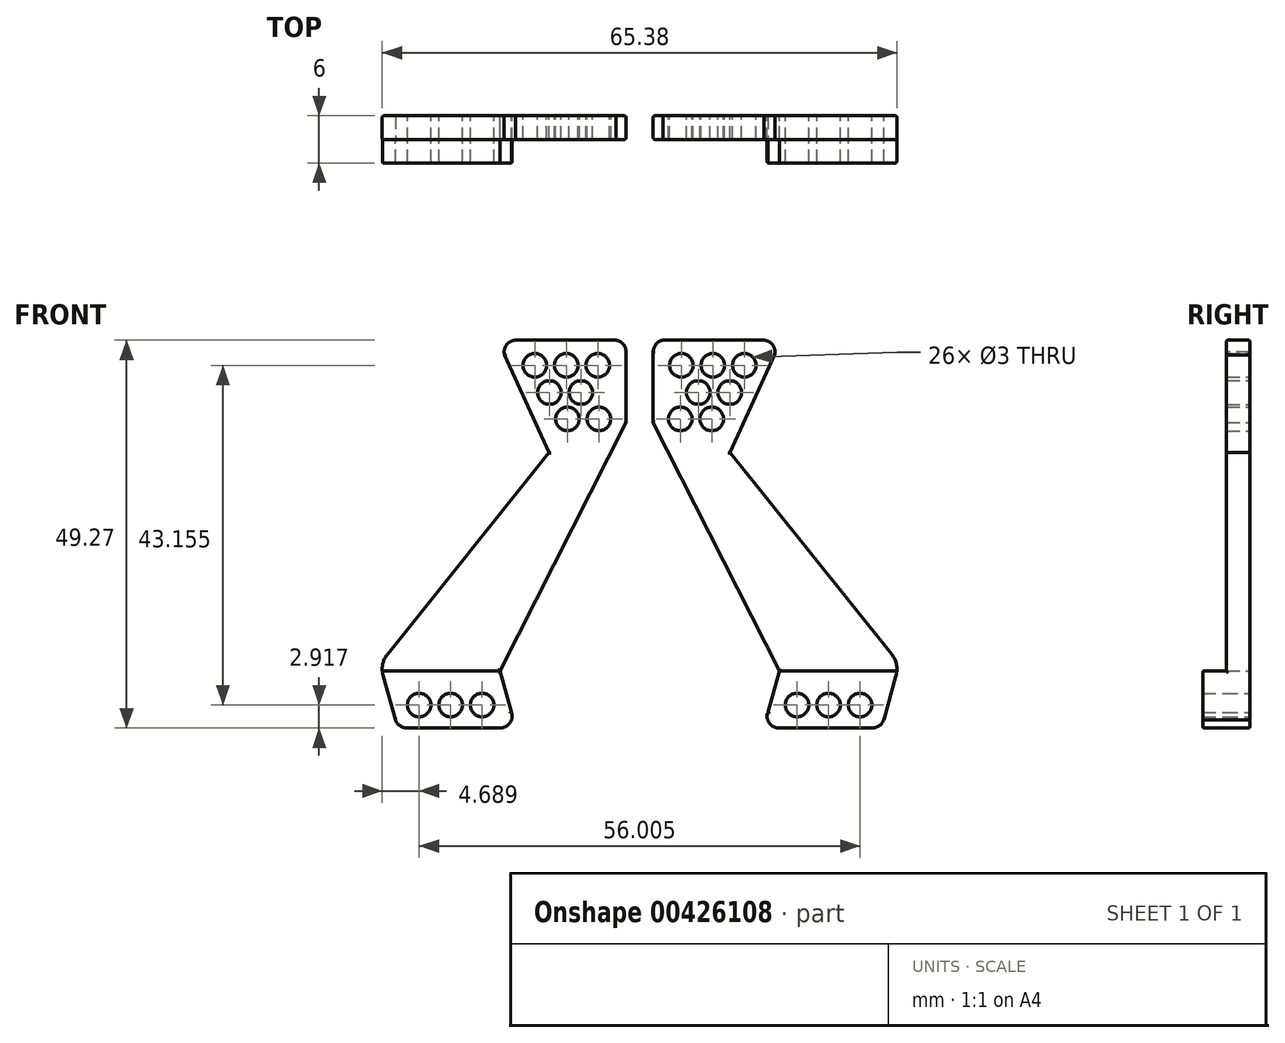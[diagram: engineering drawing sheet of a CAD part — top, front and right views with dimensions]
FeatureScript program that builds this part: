
annotation { "Feature Type Name" : "Feature", "Feature Type Description" : "" }
export const myFeature = defineFeature(function(context is Context, id is Id, definition is map)
    precondition{}
    {
        {
            var Q0;
            Q0=qCreatedBy(makeId("Front.planeOp"),FACE);
            var sketch = newSketch(context, id + "F0", { "sketchPlane" : qUnion([Q0])});
            skCircle(sketch, "E0", {"center": v(10.12, 2.98) * mm, "radius": 1.5 * mm});
            skCircle(sketch, "E1", {"center": v(6.12, 2.98) * mm, "radius": 1.5 * mm});
            skCircle(sketch, "E2", {"center": v(2.12, 2.98) * mm, "radius": 1.5 * mm});
            skCircle(sketch, "E3", {"center": v(24.82, 46.13) * mm, "radius": 1.5 * mm});
            skCircle(sketch, "E4", {"center": v(20.82, 46.13) * mm, "radius": 1.5 * mm});
            skCircle(sketch, "E5", {"center": v(16.82, 46.13) * mm, "radius": 1.5 * mm});
            skCircle(sketch, "E6", {"center": v(22.66, 42.68) * mm, "radius": 1.5 * mm});
            skCircle(sketch, "E7", {"center": v(18.66, 42.68) * mm, "radius": 1.5 * mm});
            skCircle(sketch, "E8", {"center": v(24.96, 39.32) * mm, "radius": 1.5 * mm});
            skCircle(sketch, "E9", {"center": v(20.96, 39.32) * mm, "radius": 1.5 * mm});
            skLineSegment(sketch, "E10", {"start": v(12.52, 0.07) * mm, "end": v(0.53, 0.07) * mm});
            skLineSegment(sketch, "E11", {"start": v(-1.9, 9.43) * mm, "end": v(18.64, 35.03) * mm});
            skLineSegment(sketch, "E12", {"start": v(12.97, 47.43) * mm, "end": v(18.64, 35.03) * mm});
            skLineSegment(sketch, "E13", {"start": v(14.33, 49.33) * mm, "end": v(27.15, 49.33) * mm});
            skLineSegment(sketch, "E14", {"start": v(28.4, 47.87) * mm, "end": v(28.4, 38.89) * mm});
            skLineSegment(sketch, "E15", {"start": v(28.4, 38.89) * mm, "end": v(12.38, 7.33) * mm});
            skLineSegment(sketch, "E16", {"start": v(12.38, 7.33) * mm, "end": v(13.9, 1.87) * mm});
            skArc(sketch, "E17", {"start": v(0.53, 0.07) * mm, "mid": v(-0.36, 0.36) * mm, "end": v(-0.9, 1.14) * mm});
            skArc(sketch, "E18", {"start": v(13.84, 2.06) * mm, "mid": v(13.63, 0.66) * mm, "end": v(12.34, 0.07) * mm});
            skArc(sketch, "E19", {"start": v(27.14, 49.33) * mm, "mid": v(28.05, 48.81) * mm, "end": v(28.4, 47.83) * mm});
            skArc(sketch, "E20", {"start": v(12.97, 47.42) * mm, "mid": v(13.2, 48.7) * mm, "end": v(14.33, 49.33) * mm});
            skLineSegment(sketch, "E21", {"start": v(-2.46, 6.76) * mm, "end": v(-0.9, 1.12) * mm});
            skArc(sketch, "E22", {"start": v(-2.46, 6.76) * mm, "mid": v(-2.5, 8.16) * mm, "end": v(-1.9, 9.43) * mm});
            skCircle(sketch, "E23", {"center": v(50.12, 2.98) * mm, "radius": 1.5 * mm});
            skCircle(sketch, "E24", {"center": v(54.12, 2.98) * mm, "radius": 1.5 * mm});
            skCircle(sketch, "E25", {"center": v(58.12, 2.98) * mm, "radius": 1.5 * mm});
            skCircle(sketch, "E26", {"center": v(35.43, 46.13) * mm, "radius": 1.5 * mm});
            skCircle(sketch, "E27", {"center": v(39.43, 46.13) * mm, "radius": 1.5 * mm});
            skCircle(sketch, "E28", {"center": v(43.43, 46.13) * mm, "radius": 1.5 * mm});
            skCircle(sketch, "E29", {"center": v(37.58, 42.68) * mm, "radius": 1.5 * mm});
            skCircle(sketch, "E30", {"center": v(41.58, 42.68) * mm, "radius": 1.5 * mm});
            skCircle(sketch, "E31", {"center": v(35.29, 39.32) * mm, "radius": 1.5 * mm});
            skCircle(sketch, "E32", {"center": v(39.29, 39.32) * mm, "radius": 1.5 * mm});
            skLineSegment(sketch, "E33", {"start": v(47.72, 0.07) * mm, "end": v(59.71, 0.07) * mm});
            skLineSegment(sketch, "E34", {"start": v(62.15, 9.43) * mm, "end": v(41.6, 35.03) * mm});
            skLineSegment(sketch, "E35", {"start": v(47.27, 47.43) * mm, "end": v(41.6, 35.03) * mm});
            skLineSegment(sketch, "E36", {"start": v(45.91, 49.33) * mm, "end": v(33.1, 49.33) * mm});
            skLineSegment(sketch, "E37", {"start": v(31.85, 47.87) * mm, "end": v(31.85, 38.89) * mm});
            skLineSegment(sketch, "E38", {"start": v(31.85, 38.89) * mm, "end": v(47.86, 7.33) * mm});
            skLineSegment(sketch, "E39", {"start": v(47.86, 7.33) * mm, "end": v(46.35, 1.87) * mm});
            skArc(sketch, "E40", {"start": v(59.71, 0.07) * mm, "mid": v(60.6, 0.36) * mm, "end": v(61.15, 1.14) * mm});
            skArc(sketch, "E41", {"start": v(46.4, 2.06) * mm, "mid": v(46.62, 0.66) * mm, "end": v(47.9, 0.07) * mm});
            skArc(sketch, "E42", {"start": v(33.1, 49.33) * mm, "mid": v(32.2, 48.81) * mm, "end": v(31.85, 47.83) * mm});
            skArc(sketch, "E43", {"start": v(47.27, 47.42) * mm, "mid": v(47.05, 48.7) * mm, "end": v(45.91, 49.33) * mm});
            skLineSegment(sketch, "E44", {"start": v(62.7, 6.76) * mm, "end": v(61.14, 1.12) * mm});
            skArc(sketch, "E45", {"start": v(62.7, 6.76) * mm, "mid": v(62.75, 8.16) * mm, "end": v(62.15, 9.43) * mm});
            skSolve(sketch);
        }
        {
            var Q0;
            Q0=qCreatedBy(makeId("Front.planeOp"),FACE);
            var sketch = newSketch(context, id + "F1", { "sketchPlane" : qUnion([Q0])});
            skCircle(sketch, "E46", {"center": v(10.12, 2.98) * mm, "radius": 1.5 * mm});
            skCircle(sketch, "E47", {"center": v(6.12, 2.98) * mm, "radius": 1.5 * mm});
            skCircle(sketch, "E48", {"center": v(2.12, 2.98) * mm, "radius": 1.5 * mm});
            skLineSegment(sketch, "E49", {"start": v(12.52, 0.07) * mm, "end": v(0.53, 0.07) * mm});
            skLineSegment(sketch, "E50", {"start": v(12.38, 7.33) * mm, "end": v(13.9, 1.87) * mm});
            skArc(sketch, "E51", {"start": v(0.53, 0.07) * mm, "mid": v(-0.37, 0.36) * mm, "end": v(-0.9, 1.14) * mm});
            skArc(sketch, "E52", {"start": v(13.84, 2.06) * mm, "mid": v(13.62, 0.66) * mm, "end": v(12.34, 0.07) * mm});
            skLineSegment(sketch, "E53", {"start": v(-2.46, 6.76) * mm, "end": v(-0.9, 1.12) * mm});
            skLineSegment(sketch, "E54", {"start": v(12.38, 7.33) * mm, "end": v(-2.56, 7.33) * mm});
            skArc(sketch, "E55", {"start": v(-2.46, 6.76) * mm, "mid": v(-2.53, 7.04) * mm, "end": v(-2.56, 7.33) * mm});
            skCircle(sketch, "E56", {"center": v(50.12, 2.98) * mm, "radius": 1.5 * mm});
            skCircle(sketch, "E57", {"center": v(54.12, 2.98) * mm, "radius": 1.5 * mm});
            skCircle(sketch, "E58", {"center": v(58.12, 2.98) * mm, "radius": 1.5 * mm});
            skLineSegment(sketch, "E59", {"start": v(47.72, 0.07) * mm, "end": v(59.7, 0.07) * mm});
            skLineSegment(sketch, "E60", {"start": v(47.86, 7.33) * mm, "end": v(46.34, 1.87) * mm});
            skArc(sketch, "E61", {"start": v(59.7, 0.07) * mm, "mid": v(60.6, 0.36) * mm, "end": v(61.15, 1.14) * mm});
            skArc(sketch, "E62", {"start": v(46.4, 2.06) * mm, "mid": v(46.62, 0.66) * mm, "end": v(47.9, 0.07) * mm});
            skLineSegment(sketch, "E63", {"start": v(62.7, 6.76) * mm, "end": v(61.14, 1.12) * mm});
            skLineSegment(sketch, "E64", {"start": v(47.86, 7.33) * mm, "end": v(62.8, 7.33) * mm});
            skArc(sketch, "E65", {"start": v(62.7, 6.76) * mm, "mid": v(62.77, 7.04) * mm, "end": v(62.8, 7.33) * mm});
            skSolve(sketch);
        }
        {
            var Q0;
            Q0 = qSketchRegion(id + "F0", true);
            extrude(context, id + "F2", {"entities" : qUnion([Q0]), "depth" : 3 * mm});
        }
        {
            var Q0;
            Q0 = qSketchRegion(id + "F1", true);
            extrude(context, id + "F3", {"entities" : qUnion([Q0]), "operationType" : NewBodyOperationType.ADD, "depth" : 6 * mm});
        }
        {
            var Q0;
            Q0=makeQuery(id+"F2.opExtrude","CAP_FACE",FACE,{"disambiguationData":[OSD([sQuery(id+"F0.wireOp",EDGE,"E0"),sQuery(id+"F0.wireOp",EDGE,"E1"),sQuery(id+"F0.wireOp",EDGE,"E2"),sQuery(id+"F0.wireOp",EDGE,"E3"),sQuery(id+"F0.wireOp",EDGE,"E4"),sQuery(id+"F0.wireOp",EDGE,"E5"),sQuery(id+"F0.wireOp",EDGE,"E6"),sQuery(id+"F0.wireOp",EDGE,"E7"),sQuery(id+"F0.wireOp",EDGE,"E8"),sQuery(id+"F0.wireOp",EDGE,"E9"),sQuery(id+"F0.wireOp",EDGE,"E10"),sQuery(id+"F0.wireOp",EDGE,"E11"),sQuery(id+"F0.wireOp",EDGE,"E12"),sQuery(id+"F0.wireOp",EDGE,"E13"),sQuery(id+"F0.wireOp",EDGE,"E14"),sQuery(id+"F0.wireOp",EDGE,"E15"),sQuery(id+"F0.wireOp",EDGE,"E16"),sQuery(id+"F0.wireOp",EDGE,"E17"),sQuery(id+"F0.wireOp",EDGE,"E18"),sQuery(id+"F0.wireOp",EDGE,"E19"),sQuery(id+"F0.wireOp",EDGE,"E20"),sQuery(id+"F0.wireOp",EDGE,"E21"),sQuery(id+"F0.wireOp",EDGE,"E22")])],"isStart":true});
            var Q1;
            Q1=makeQuery(id+"F2.opExtrude","CAP_FACE",FACE,{"disambiguationData":[OSD([sQuery(id+"F0.wireOp",EDGE,"E23"),sQuery(id+"F0.wireOp",EDGE,"E24"),sQuery(id+"F0.wireOp",EDGE,"E25"),sQuery(id+"F0.wireOp",EDGE,"E26"),sQuery(id+"F0.wireOp",EDGE,"E27"),sQuery(id+"F0.wireOp",EDGE,"E28"),sQuery(id+"F0.wireOp",EDGE,"E29"),sQuery(id+"F0.wireOp",EDGE,"E30"),sQuery(id+"F0.wireOp",EDGE,"E31"),sQuery(id+"F0.wireOp",EDGE,"E32"),sQuery(id+"F0.wireOp",EDGE,"E33"),sQuery(id+"F0.wireOp",EDGE,"E34"),sQuery(id+"F0.wireOp",EDGE,"E35"),sQuery(id+"F0.wireOp",EDGE,"E36"),sQuery(id+"F0.wireOp",EDGE,"E37"),sQuery(id+"F0.wireOp",EDGE,"E38"),sQuery(id+"F0.wireOp",EDGE,"E39"),sQuery(id+"F0.wireOp",EDGE,"E40"),sQuery(id+"F0.wireOp",EDGE,"E41"),sQuery(id+"F0.wireOp",EDGE,"E42"),sQuery(id+"F0.wireOp",EDGE,"E43"),sQuery(id+"F0.wireOp",EDGE,"E44"),sQuery(id+"F0.wireOp",EDGE,"E45")])],"isStart":true});
            var Q2;
            Q2=makeQuery(id+"F3.opExtrude","CAP_FACE",FACE,{"disambiguationData":[OSD([sQuery(id+"F1.wireOp",EDGE,"E46"),sQuery(id+"F1.wireOp",EDGE,"E47"),sQuery(id+"F1.wireOp",EDGE,"E48"),sQuery(id+"F1.wireOp",EDGE,"E49"),sQuery(id+"F1.wireOp",EDGE,"E50"),sQuery(id+"F1.wireOp",EDGE,"E51"),sQuery(id+"F1.wireOp",EDGE,"E52"),sQuery(id+"F1.wireOp",EDGE,"E53"),sQuery(id+"F1.wireOp",EDGE,"E54"),sQuery(id+"F1.wireOp",EDGE,"E55")])],"isStart":false});
            var Q3;
            Q3=makeQuery(id+"F3.opExtrude","CAP_FACE",FACE,{"disambiguationData":[OSD([sQuery(id+"F1.wireOp",EDGE,"E56"),sQuery(id+"F1.wireOp",EDGE,"E57"),sQuery(id+"F1.wireOp",EDGE,"E58"),sQuery(id+"F1.wireOp",EDGE,"E59"),sQuery(id+"F1.wireOp",EDGE,"E60"),sQuery(id+"F1.wireOp",EDGE,"E61"),sQuery(id+"F1.wireOp",EDGE,"E62"),sQuery(id+"F1.wireOp",EDGE,"E63"),sQuery(id+"F1.wireOp",EDGE,"E64"),sQuery(id+"F1.wireOp",EDGE,"E65")])],"isStart":false});
            var Q4;
            Q4=makeQuery(id+"F3.opExtrude","SWEPT_EDGE",EDGE,{"disambiguationData":[OSD([sQuery(id+"F1.wireOp",EDGE,"E64"),sQuery(id+"F1.wireOp",EDGE,"E65")])]});
            var Q5;
            {var subQ0=sQuery(id+"F0.wireOp",EDGE,"E45");Q5=makeQuery(id+"F3.boolean.opBoolean","SPLIT",EDGE,{"disambiguationData":[topologyDisambiguationEdgeConnected([makeQuery(id+"F2.opExtrude","CAP_FACE",FACE,{"disambiguationData":[OSD([sQuery(id+"F0.wireOp",EDGE,"E23"),sQuery(id+"F0.wireOp",EDGE,"E24"),sQuery(id+"F0.wireOp",EDGE,"E25"),sQuery(id+"F0.wireOp",EDGE,"E26"),sQuery(id+"F0.wireOp",EDGE,"E27"),sQuery(id+"F0.wireOp",EDGE,"E28"),sQuery(id+"F0.wireOp",EDGE,"E29"),sQuery(id+"F0.wireOp",EDGE,"E30"),sQuery(id+"F0.wireOp",EDGE,"E31"),sQuery(id+"F0.wireOp",EDGE,"E32"),sQuery(id+"F0.wireOp",EDGE,"E33"),sQuery(id+"F0.wireOp",EDGE,"E34"),sQuery(id+"F0.wireOp",EDGE,"E35"),sQuery(id+"F0.wireOp",EDGE,"E36"),sQuery(id+"F0.wireOp",EDGE,"E37"),sQuery(id+"F0.wireOp",EDGE,"E38"),sQuery(id+"F0.wireOp",EDGE,"E39"),sQuery(id+"F0.wireOp",EDGE,"E40"),sQuery(id+"F0.wireOp",EDGE,"E41"),sQuery(id+"F0.wireOp",EDGE,"E42"),sQuery(id+"F0.wireOp",EDGE,"E43"),sQuery(id+"F0.wireOp",EDGE,"E44"),subQ0])],"isStart":false})])],"derivedFrom":makeQuery(id+"F2.opExtrude","CAP_EDGE",EDGE,{"disambiguationData":[OSD([subQ0])],"isStart":false})});}
            var Q6;
            Q6=makeQuery(id+"F2.opExtrude","CAP_EDGE",EDGE,{"disambiguationData":[OSD([sQuery(id+"F0.wireOp",EDGE,"E34")])],"isStart":false});
            var Q7;
            Q7=makeQuery(id+"F2.opExtrude","CAP_EDGE",EDGE,{"disambiguationData":[OSD([sQuery(id+"F0.wireOp",EDGE,"E35")])],"isStart":false});
            var Q8;
            Q8=makeQuery(id+"F2.opExtrude","CAP_EDGE",EDGE,{"disambiguationData":[OSD([sQuery(id+"F0.wireOp",EDGE,"E43")])],"isStart":false});
            var Q9;
            Q9=makeQuery(id+"F2.opExtrude","CAP_EDGE",EDGE,{"disambiguationData":[OSD([sQuery(id+"F0.wireOp",EDGE,"E36")])],"isStart":false});
            var Q10;
            Q10=makeQuery(id+"F2.opExtrude","CAP_EDGE",EDGE,{"disambiguationData":[OSD([sQuery(id+"F0.wireOp",EDGE,"E42")])],"isStart":false});
            var Q11;
            Q11=makeQuery(id+"F2.opExtrude","CAP_EDGE",EDGE,{"disambiguationData":[OSD([sQuery(id+"F0.wireOp",EDGE,"E37")])],"isStart":false});
            var Q12;
            Q12=makeQuery(id+"F2.opExtrude","CAP_EDGE",EDGE,{"disambiguationData":[OSD([sQuery(id+"F0.wireOp",EDGE,"E38")])],"isStart":false});
            var Q13;
            Q13=makeQuery(id+"F2.opExtrude","CAP_EDGE",EDGE,{"disambiguationData":[OSD([sQuery(id+"F0.wireOp",EDGE,"E15")])],"isStart":false});
            var Q14;
            Q14=makeQuery(id+"F2.opExtrude","CAP_EDGE",EDGE,{"disambiguationData":[OSD([sQuery(id+"F0.wireOp",EDGE,"E14")])],"isStart":false});
            var Q15;
            Q15=makeQuery(id+"F2.opExtrude","CAP_EDGE",EDGE,{"disambiguationData":[OSD([sQuery(id+"F0.wireOp",EDGE,"E19")])],"isStart":false});
            var Q16;
            Q16=makeQuery(id+"F2.opExtrude","CAP_EDGE",EDGE,{"disambiguationData":[OSD([sQuery(id+"F0.wireOp",EDGE,"E13")])],"isStart":false});
            var Q17;
            Q17=makeQuery(id+"F2.opExtrude","CAP_EDGE",EDGE,{"disambiguationData":[OSD([sQuery(id+"F0.wireOp",EDGE,"E20")])],"isStart":false});
            var Q18;
            Q18=makeQuery(id+"F2.opExtrude","CAP_EDGE",EDGE,{"disambiguationData":[OSD([sQuery(id+"F0.wireOp",EDGE,"E12")])],"isStart":false});
            var Q19;
            Q19=makeQuery(id+"F2.opExtrude","CAP_EDGE",EDGE,{"disambiguationData":[OSD([sQuery(id+"F0.wireOp",EDGE,"E11")])],"isStart":false});
            var Q20;
            Q20=makeQuery(id+"F3.opExtrude","SWEPT_EDGE",EDGE,{"disambiguationData":[OSD([sQuery(id+"F1.wireOp",EDGE,"E54"),sQuery(id+"F1.wireOp",EDGE,"E55")])]});
            var Q21;
            Q21=makeQuery(id+"F2.opExtrude","CAP_EDGE",EDGE,{"disambiguationData":[OSD([sQuery(id+"F0.wireOp",EDGE,"E5")])],"isStart":false});
            var Q22;
            Q22=makeQuery(id+"F2.opExtrude","CAP_EDGE",EDGE,{"disambiguationData":[OSD([sQuery(id+"F0.wireOp",EDGE,"E4")])],"isStart":false});
            var Q23;
            Q23=makeQuery(id+"F2.opExtrude","CAP_EDGE",EDGE,{"disambiguationData":[OSD([sQuery(id+"F0.wireOp",EDGE,"E3")])],"isStart":false});
            var Q24;
            Q24=makeQuery(id+"F2.opExtrude","CAP_EDGE",EDGE,{"disambiguationData":[OSD([sQuery(id+"F0.wireOp",EDGE,"E6")])],"isStart":false});
            var Q25;
            Q25=makeQuery(id+"F2.opExtrude","CAP_EDGE",EDGE,{"disambiguationData":[OSD([sQuery(id+"F0.wireOp",EDGE,"E7")])],"isStart":false});
            var Q26;
            Q26=makeQuery(id+"F2.opExtrude","CAP_EDGE",EDGE,{"disambiguationData":[OSD([sQuery(id+"F0.wireOp",EDGE,"E9")])],"isStart":false});
            var Q27;
            Q27=makeQuery(id+"F2.opExtrude","CAP_EDGE",EDGE,{"disambiguationData":[OSD([sQuery(id+"F0.wireOp",EDGE,"E8")])],"isStart":false});
            var Q28;
            Q28=makeQuery(id+"F2.opExtrude","CAP_EDGE",EDGE,{"disambiguationData":[OSD([sQuery(id+"F0.wireOp",EDGE,"E31")])],"isStart":false});
            var Q29;
            Q29=makeQuery(id+"F2.opExtrude","CAP_EDGE",EDGE,{"disambiguationData":[OSD([sQuery(id+"F0.wireOp",EDGE,"E26")])],"isStart":false});
            var Q30;
            Q30=makeQuery(id+"F2.opExtrude","CAP_EDGE",EDGE,{"disambiguationData":[OSD([sQuery(id+"F0.wireOp",EDGE,"E27")])],"isStart":false});
            var Q31;
            Q31=makeQuery(id+"F2.opExtrude","CAP_EDGE",EDGE,{"disambiguationData":[OSD([sQuery(id+"F0.wireOp",EDGE,"E29")])],"isStart":false});
            var Q32;
            Q32=makeQuery(id+"F2.opExtrude","CAP_EDGE",EDGE,{"disambiguationData":[OSD([sQuery(id+"F0.wireOp",EDGE,"E32")])],"isStart":false});
            var Q33;
            Q33=makeQuery(id+"F2.opExtrude","CAP_EDGE",EDGE,{"disambiguationData":[OSD([sQuery(id+"F0.wireOp",EDGE,"E30")])],"isStart":false});
            var Q34;
            Q34=makeQuery(id+"F2.opExtrude","CAP_EDGE",EDGE,{"disambiguationData":[OSD([sQuery(id+"F0.wireOp",EDGE,"E28")])],"isStart":false});
            fillet(context, id + "F4", {"entities" : qUnion([Q0, Q1, Q2, Q3, Q4, Q5, Q6, Q7, Q8, Q9, Q10, Q11, Q12, Q13, Q14, Q15, Q16, Q17, Q18, Q19, Q20, Q21, Q22, Q23, Q24, Q25, Q26, Q27, Q28, Q29, Q30, Q31, Q32, Q33, Q34]), "radius" : .2 * mm, "tangentPropagation" : true, "allowEdgeOverflow" : false});
        }
    });
